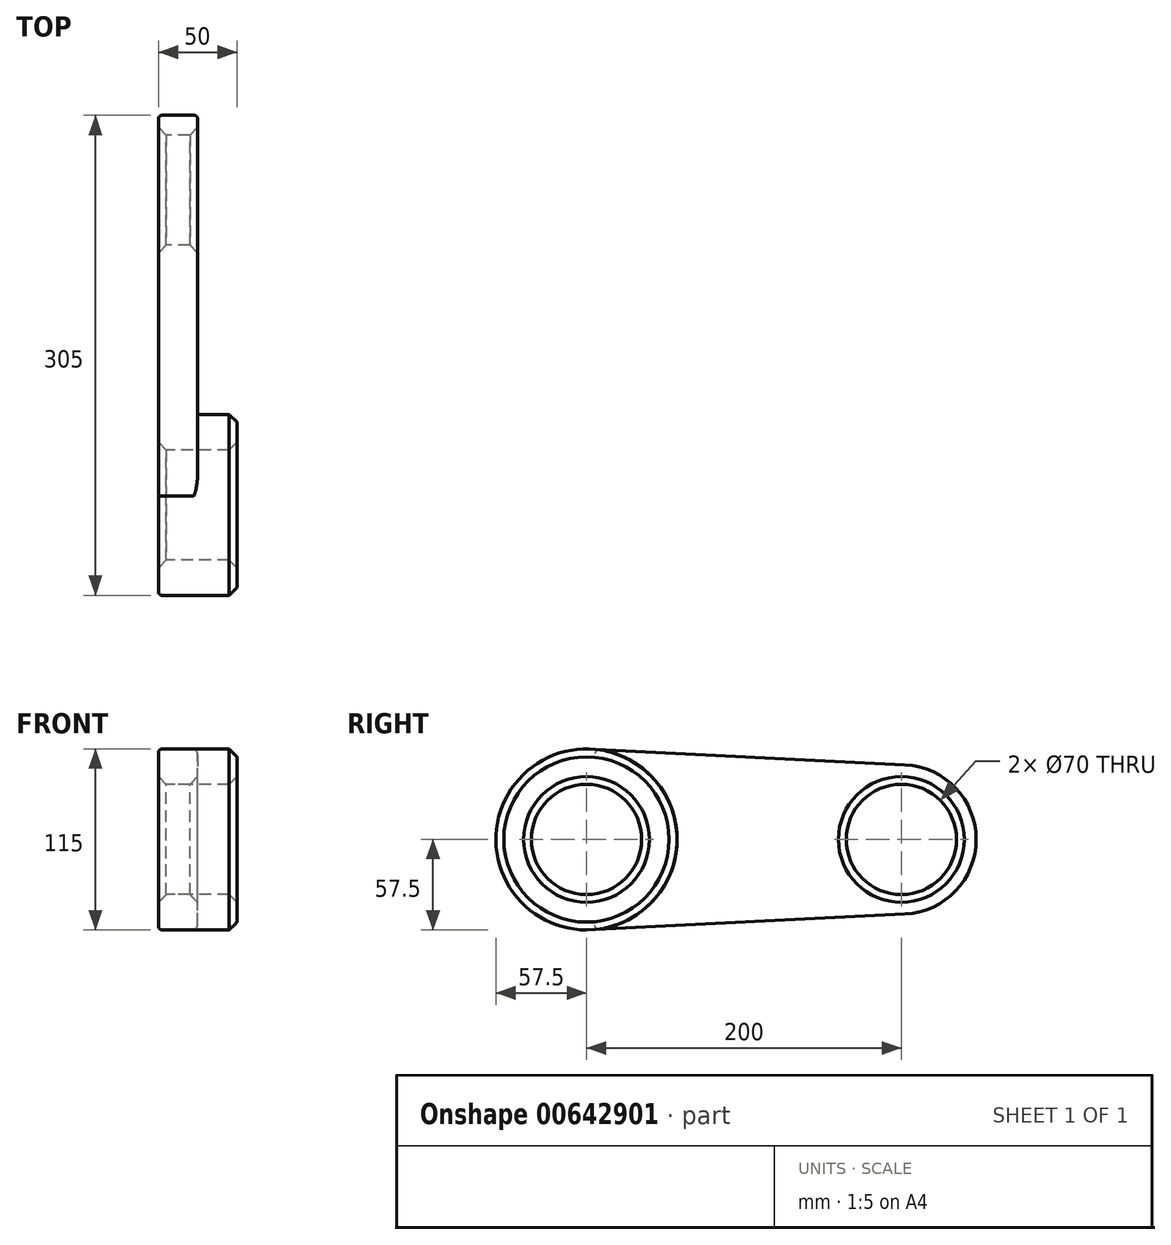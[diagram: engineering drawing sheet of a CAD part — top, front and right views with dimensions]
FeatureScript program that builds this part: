
annotation { "Feature Type Name" : "Feature", "Feature Type Description" : "" }
export const myFeature = defineFeature(function(context is Context, id is Id, definition is map)
    precondition{}
    {
        {
            var Q0;
            Q0=qCreatedBy(makeId("Right.planeOp"),FACE);
            var sketch = newSketch(context, id + "F0", { "sketchPlane" : qUnion([Q0])});
            skCircle(sketch, "E0", {"center": v(0, 0) * mm, "radius": 57.5 * mm});
            skCircle(sketch, "E1", {"center": v(200, 0) * mm, "radius": 47.5 * mm});
            skLineSegment(sketch, "E2", {"start": v(0, 57.5) * mm, "end": v(202.36, 47.44) * mm});
            skLineSegment(sketch, "E3", {"start": v(202.36, 47.44) * mm, "end": v(202.36, 47.44) * mm});
            skLineSegment(sketch, "E4", {"start": v(0, -57.5) * mm, "end": v(202.36, -47.44) * mm});
            skCircle(sketch, "E5", {"center": v(0, 0) * mm, "radius": 35 * mm});
            skCircle(sketch, "E6", {"center": v(200, 0) * mm, "radius": 35 * mm});
            skSolve(sketch);
        }
        {
            var Q0;
            Q0=qSketchRegion(id+"F0",true);
            extrude(context, id + "F1", {"entities" : qUnion([Q0]), "depth" : 25 * mm, "offsetDistance" : 25 * mm});
        }
        {
            var Q0;
            Q0=qCreatedBy(makeId("Right.planeOp"),FACE);
            var sketch = newSketch(context, id + "F2", { "sketchPlane" : qUnion([Q0])});
            skCircle(sketch, "E7", {"center": v(0, 0) * mm, "radius": 57.5 * mm});
            skCircle(sketch, "E8", {"center": v(0, 0) * mm, "radius": 35 * mm});
            skSolve(sketch);
        }
        {
            var Q0;
            Q0=qSketchRegion(id+"F2",true);
            extrude(context, id + "F3", {"entities" : qUnion([Q0]), "operationType" : NewBodyOperationType.ADD, "depth" : 50 * mm, "offsetDistance" : 25 * mm});
        }
        {
            var Q0;
            Q0=makeQuery(id+"F3.opExtrude","CAP_EDGE",EDGE,{"disambiguationData":[OSD([sQuery(id+"F2.wireOp",EDGE,"E8")])],"isStart":false});
            var Q1;
            Q1=makeQuery(id+"F3.opExtrude","CAP_EDGE",EDGE,{"disambiguationData":[OSD([sQuery(id+"F2.wireOp",EDGE,"E7")])],"isStart":false});
            var Q2;
            Q2=makeQuery(id+"F1.opExtrude","CAP_EDGE",EDGE,{"disambiguationData":[OSD([sQuery(id+"F0.wireOp",EDGE,"E6")])],"isStart":false});
            chamfer(context, id + "F4", {"entities" : qUnion([Q0, Q1, Q2]), "width" : 5 * mm, "tangentPropagation" : true});
        }
        {
            var Q0;
            Q0=makeQuery(id+"F1.opExtrude","CAP_EDGE",EDGE,{"disambiguationData":[OSD([sQuery(id+"F0.wireOp",EDGE,"E6")])],"isStart":true});
            var Q1;
            Q1=makeQuery(id+"F1.opExtrude","CAP_EDGE",EDGE,{"disambiguationData":[OSD([sQuery(id+"F0.wireOp",EDGE,"E5")])],"isStart":true});
            chamfer(context, id + "F5", {"entities" : qUnion([Q0, Q1]), "width" : 5 * mm, "tangentPropagation" : true});
        }
        {
            var Q0;
            Q0=makeQuery(id+"F1.opExtrude","CAP_EDGE",EDGE,{"disambiguationData":[OSD([sQuery(id+"F0.wireOp",EDGE,"E0")])],"isStart":true});
            var Q1;
            Q1=makeQuery(id+"F1.opExtrude","CAP_EDGE",EDGE,{"disambiguationData":[OSD([sQuery(id+"F0.wireOp",EDGE,"E4")])],"isStart":true});
            var Q2;
            Q2=makeQuery(id+"F1.opExtrude","CAP_EDGE",EDGE,{"disambiguationData":[OSD([sQuery(id+"F0.wireOp",EDGE,"E2")])],"isStart":true});
            var Q3;
            Q3=makeQuery(id+"F1.opExtrude","CAP_EDGE",EDGE,{"disambiguationData":[OSD([sQuery(id+"F0.wireOp",EDGE,"E1")])],"isStart":true});
            var Q4;
            Q4=makeQuery(id+"F1.opExtrude","CAP_EDGE",EDGE,{"disambiguationData":[OSD([sQuery(id+"F0.wireOp",EDGE,"E2")])],"isStart":false});
            var Q5;
            Q5=makeQuery(id+"F1.opExtrude","CAP_EDGE",EDGE,{"disambiguationData":[OSD([sQuery(id+"F0.wireOp",EDGE,"E1")])],"isStart":false});
            var Q6;
            Q6=makeQuery(id+"F1.opExtrude","CAP_EDGE",EDGE,{"disambiguationData":[OSD([sQuery(id+"F0.wireOp",EDGE,"E4")])],"isStart":false});
            fillet(context, id + "F6", {"entities" : qUnion([Q0, Q1, Q2, Q3, Q4, Q5, Q6]), "radius" : 2.5 * mm, "tangentPropagation" : true, "allowEdgeOverflow" : false});
        }
    });
